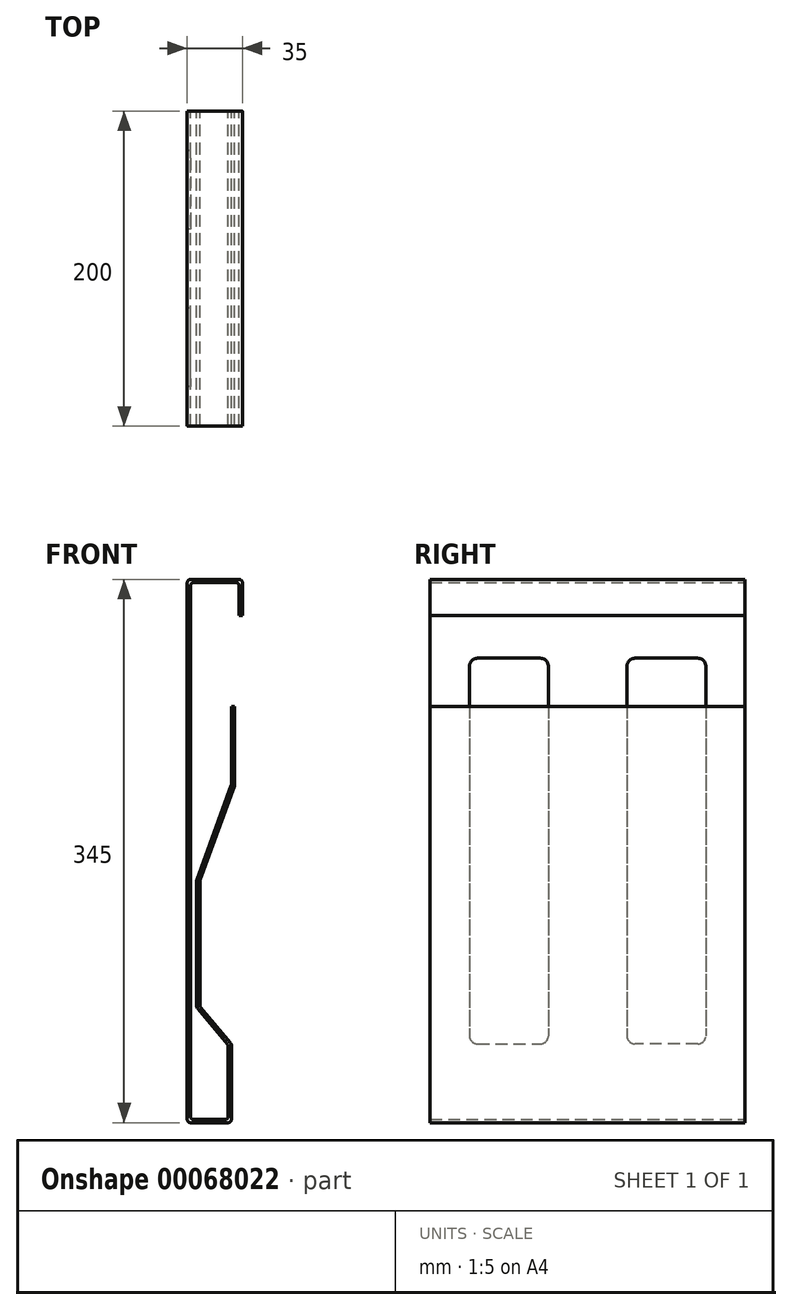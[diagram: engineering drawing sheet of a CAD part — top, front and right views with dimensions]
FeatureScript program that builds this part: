
annotation { "Feature Type Name" : "Feature", "Feature Type Description" : "" }
export const myFeature = defineFeature(function(context is Context, id is Id, definition is map)
    precondition{}
    {
        {
            var Q0;
            Q0=qCreatedBy(makeId("Front.planeOp"),FACE);
            var sketch = newSketch(context, id + "F0", { "sketchPlane" : qUnion([Q0])});
            skLineSegment(sketch, "E0", {"start": v(0, 0) * mm, "end": v(35, 0) * mm});
            skLineSegment(sketch, "E1", {"start": v(35, 0) * mm, "end": v(35, -23) * mm});
            skLineSegment(sketch, "E2", {"start": v(0, 0) * mm, "end": v(0, -345) * mm});
            skLineSegment(sketch, "E3", {"start": v(0, -345) * mm, "end": v(28, -345) * mm});
            skLineSegment(sketch, "E4", {"start": v(28, -295) * mm, "end": v(28, -345) * mm});
            skLineSegment(sketch, "E5.0", {"start": v(33, -2) * mm, "end": v(33, -23) * mm});
            skLineSegment(sketch, "E5.1", {"start": v(26, -295.73) * mm, "end": v(26, -343) * mm});
            skLineSegment(sketch, "E5.2", {"start": v(2, -343) * mm, "end": v(26, -343) * mm});
            skLineSegment(sketch, "E5.3", {"start": v(2, -2) * mm, "end": v(2, -343) * mm});
            skLineSegment(sketch, "E5.4", {"start": v(2, -2) * mm, "end": v(33, -2) * mm});
            skLineSegment(sketch, "E6", {"start": v(33, -23) * mm, "end": v(35, -23) * mm});
            skLineSegment(sketch, "E7", {"start": v(26, -295.73) * mm, "end": v(6, -271.9) * mm});
            skLineSegment(sketch, "E8", {"start": v(6, -271.9) * mm, "end": v(6, -190.81) * mm});
            skLineSegment(sketch, "E9", {"start": v(6, -190.81) * mm, "end": v(28, -130.37) * mm});
            skLineSegment(sketch, "E10", {"start": v(28, -130.37) * mm, "end": v(28, -80.72) * mm});
            skLineSegment(sketch, "E11.0", {"start": v(30, -130.72) * mm, "end": v(30, -80.72) * mm});
            skLineSegment(sketch, "E11.1", {"start": v(8, -191.16) * mm, "end": v(30, -130.72) * mm});
            skLineSegment(sketch, "E11.2", {"start": v(8, -271.16) * mm, "end": v(8, -191.16) * mm});
            skLineSegment(sketch, "E11.3", {"start": v(28, -295) * mm, "end": v(8, -271.16) * mm});
            skLineSegment(sketch, "E12", {"start": v(28, -80.72) * mm, "end": v(30, -80.72) * mm});
            skSolve(sketch);
        }
        {
            var Q0;
            Q0=qSketchRegion(id+"F0",true);
            extrude(context, id + "F1", {"entities" : qUnion([Q0]), "depth" : 200 * mm});
        }
        {
            var Q0;
            Q0=makeQuery(id+"F1.opExtrude","SWEPT_EDGE",EDGE,{"disambiguationData":[OSD([sQuery(id+"F0.wireOp",EDGE,"E0"),sQuery(id+"F0.wireOp",EDGE,"E2")])]});
            var Q1;
            Q1=makeQuery(id+"F1.opExtrude","SWEPT_EDGE",EDGE,{"disambiguationData":[OSD([sQuery(id+"F0.wireOp",EDGE,"E0"),sQuery(id+"F0.wireOp",EDGE,"E1")])]});
            var Q2;
            Q2=makeQuery(id+"F1.opExtrude","SWEPT_EDGE",EDGE,{"disambiguationData":[OSD([sQuery(id+"F0.wireOp",EDGE,"E5.0"),sQuery(id+"F0.wireOp",EDGE,"E5.4")])]});
            var Q3;
            Q3=makeQuery(id+"F1.opExtrude","SWEPT_EDGE",EDGE,{"disambiguationData":[OSD([sQuery(id+"F0.wireOp",EDGE,"E5.3"),sQuery(id+"F0.wireOp",EDGE,"E5.4")])]});
            var Q4;
            Q4=makeQuery(id+"F1.opExtrude","SWEPT_EDGE",EDGE,{"disambiguationData":[OSD([sQuery(id+"F0.wireOp",EDGE,"E2"),sQuery(id+"F0.wireOp",EDGE,"E3")])]});
            var Q5;
            Q5=makeQuery(id+"F1.opExtrude","SWEPT_EDGE",EDGE,{"disambiguationData":[OSD([sQuery(id+"F0.wireOp",EDGE,"E5.2"),sQuery(id+"F0.wireOp",EDGE,"E5.3")])]});
            var Q6;
            Q6=makeQuery(id+"F1.opExtrude","SWEPT_EDGE",EDGE,{"disambiguationData":[OSD([sQuery(id+"F0.wireOp",EDGE,"E3"),sQuery(id+"F0.wireOp",EDGE,"E4")])]});
            var Q7;
            Q7=makeQuery(id+"F1.opExtrude","SWEPT_EDGE",EDGE,{"disambiguationData":[OSD([sQuery(id+"F0.wireOp",EDGE,"E5.1"),sQuery(id+"F0.wireOp",EDGE,"E5.2")])]});
            var Q8;
            Q8=makeQuery(id+"F1.opExtrude","SWEPT_EDGE",EDGE,{"disambiguationData":[OSD([sQuery(id+"F0.wireOp",EDGE,"E5.1"),sQuery(id+"F0.wireOp",EDGE,"E7")])]});
            var Q9;
            Q9=makeQuery(id+"F1.opExtrude","SWEPT_EDGE",EDGE,{"disambiguationData":[OSD([sQuery(id+"F0.wireOp",EDGE,"E4"),sQuery(id+"F0.wireOp",EDGE,"E11.3")])]});
            var Q10;
            Q10=makeQuery(id+"F1.opExtrude","SWEPT_EDGE",EDGE,{"disambiguationData":[OSD([sQuery(id+"F0.wireOp",EDGE,"E11.2"),sQuery(id+"F0.wireOp",EDGE,"E11.3")])]});
            var Q11;
            Q11=makeQuery(id+"F1.opExtrude","SWEPT_EDGE",EDGE,{"disambiguationData":[OSD([sQuery(id+"F0.wireOp",EDGE,"E7"),sQuery(id+"F0.wireOp",EDGE,"E8")])]});
            var Q12;
            Q12=makeQuery(id+"F1.opExtrude","SWEPT_EDGE",EDGE,{"disambiguationData":[OSD([sQuery(id+"F0.wireOp",EDGE,"E8"),sQuery(id+"F0.wireOp",EDGE,"E9")])]});
            var Q13;
            Q13=makeQuery(id+"F1.opExtrude","SWEPT_EDGE",EDGE,{"disambiguationData":[OSD([sQuery(id+"F0.wireOp",EDGE,"E11.1"),sQuery(id+"F0.wireOp",EDGE,"E11.2")])]});
            var Q14;
            Q14=makeQuery(id+"F1.opExtrude","SWEPT_EDGE",EDGE,{"disambiguationData":[OSD([sQuery(id+"F0.wireOp",EDGE,"E11.0"),sQuery(id+"F0.wireOp",EDGE,"E11.1")])]});
            var Q15;
            Q15=makeQuery(id+"F1.opExtrude","SWEPT_EDGE",EDGE,{"disambiguationData":[OSD([sQuery(id+"F0.wireOp",EDGE,"E9"),sQuery(id+"F0.wireOp",EDGE,"E10")])]});
            fillet(context, id + "F2", {"entities" : qUnion([Q0, Q1, Q2, Q3, Q4, Q5, Q6, Q7, Q8, Q9, Q10, Q11, Q12, Q13, Q14, Q15]), "radius" : 2 * mm, "tangentPropagation" : true, "allowEdgeOverflow" : false});
        }
        {
            var Q0;
            Q0=makeQuery(id+"F1.opExtrude","SWEPT_FACE",FACE,{"disambiguationData":[OSD([sQuery(id+"F0.wireOp",EDGE,"E2")])]});
            var sketch = newSketch(context, id + "F3", { "sketchPlane" : qUnion([Q0])});
            skLineSegment(sketch, "E13", {"start": v(100, -2) * mm, "end": v(100, -31.04) * mm, "construction": true});
            skLineSegment(sketch, "E14.bottom", {"start": v(30, -50) * mm, "end": v(70, -50) * mm});
            skLineSegment(sketch, "E14.top", {"start": v(30, -295) * mm, "end": v(70, -295) * mm});
            skLineSegment(sketch, "E14.left", {"start": v(25, -55) * mm, "end": v(25, -290) * mm});
            skLineSegment(sketch, "E14.right", {"start": v(75, -55) * mm, "end": v(75, -290) * mm});
            skPoint(sketch, "E15.visualSharp", {"position": v(25, -50) * mm});
            skArc(sketch, "E15.filletArc", {"start": v(30, -50) * mm, "mid": v(26.46, -51.46) * mm, "end": v(25, -55) * mm});
            skPoint(sketch, "E16.visualSharp", {"position": v(75, -50) * mm});
            skArc(sketch, "E16.filletArc", {"start": v(75, -55) * mm, "mid": v(73.54, -51.46) * mm, "end": v(70, -50) * mm});
            skPoint(sketch, "E17.visualSharp", {"position": v(75, -295) * mm});
            skArc(sketch, "E17.filletArc", {"start": v(70, -295) * mm, "mid": v(73.54, -293.54) * mm, "end": v(75, -290) * mm});
            skPoint(sketch, "E18.visualSharp", {"position": v(25, -295) * mm});
            skArc(sketch, "E18.filletArc", {"start": v(25, -290) * mm, "mid": v(26.46, -293.54) * mm, "end": v(30, -295) * mm});
            skArc(sketch, "E19.MirrorCS", {"start": v(170, -50) * mm, "mid": v(173.54, -51.46) * mm, "end": v(175, -55) * mm});
            skArc(sketch, "E20.MirrorCS", {"start": v(125, -55) * mm, "mid": v(126.46, -51.46) * mm, "end": v(130, -50) * mm});
            skArc(sketch, "E21.MirrorCS", {"start": v(175, -290) * mm, "mid": v(173.54, -293.54) * mm, "end": v(170, -295) * mm});
            skArc(sketch, "E22.MirrorCS", {"start": v(130, -295) * mm, "mid": v(126.46, -293.54) * mm, "end": v(125, -290) * mm});
            skPoint(sketch, "E23.MirrorP", {"position": v(175, -295) * mm});
            skLineSegment(sketch, "E24.MirrorCS", {"start": v(125, -55) * mm, "end": v(125, -290) * mm});
            skPoint(sketch, "E25.MirrorP", {"position": v(125, -50) * mm});
            skPoint(sketch, "E26.MirrorP", {"position": v(175, -50) * mm});
            skLineSegment(sketch, "E27.MirrorCS", {"start": v(170, -50) * mm, "end": v(130, -50) * mm});
            skPoint(sketch, "E28.MirrorP", {"position": v(125, -295) * mm});
            skLineSegment(sketch, "E29.MirrorCS", {"start": v(170, -295) * mm, "end": v(130, -295) * mm});
            skLineSegment(sketch, "E30.MirrorCS", {"start": v(175, -55) * mm, "end": v(175, -290) * mm});
            skSolve(sketch);
        }
        {
            var Q0;
            Q0 = qSketchRegion(id + "F3", true);
            extrude(context, id + "F4", {"entities" : qUnion([Q0]), "operationType" : NewBodyOperationType.REMOVE, "oppositeDirection" : true, "depth" : 2 * mm});
        }
    });
